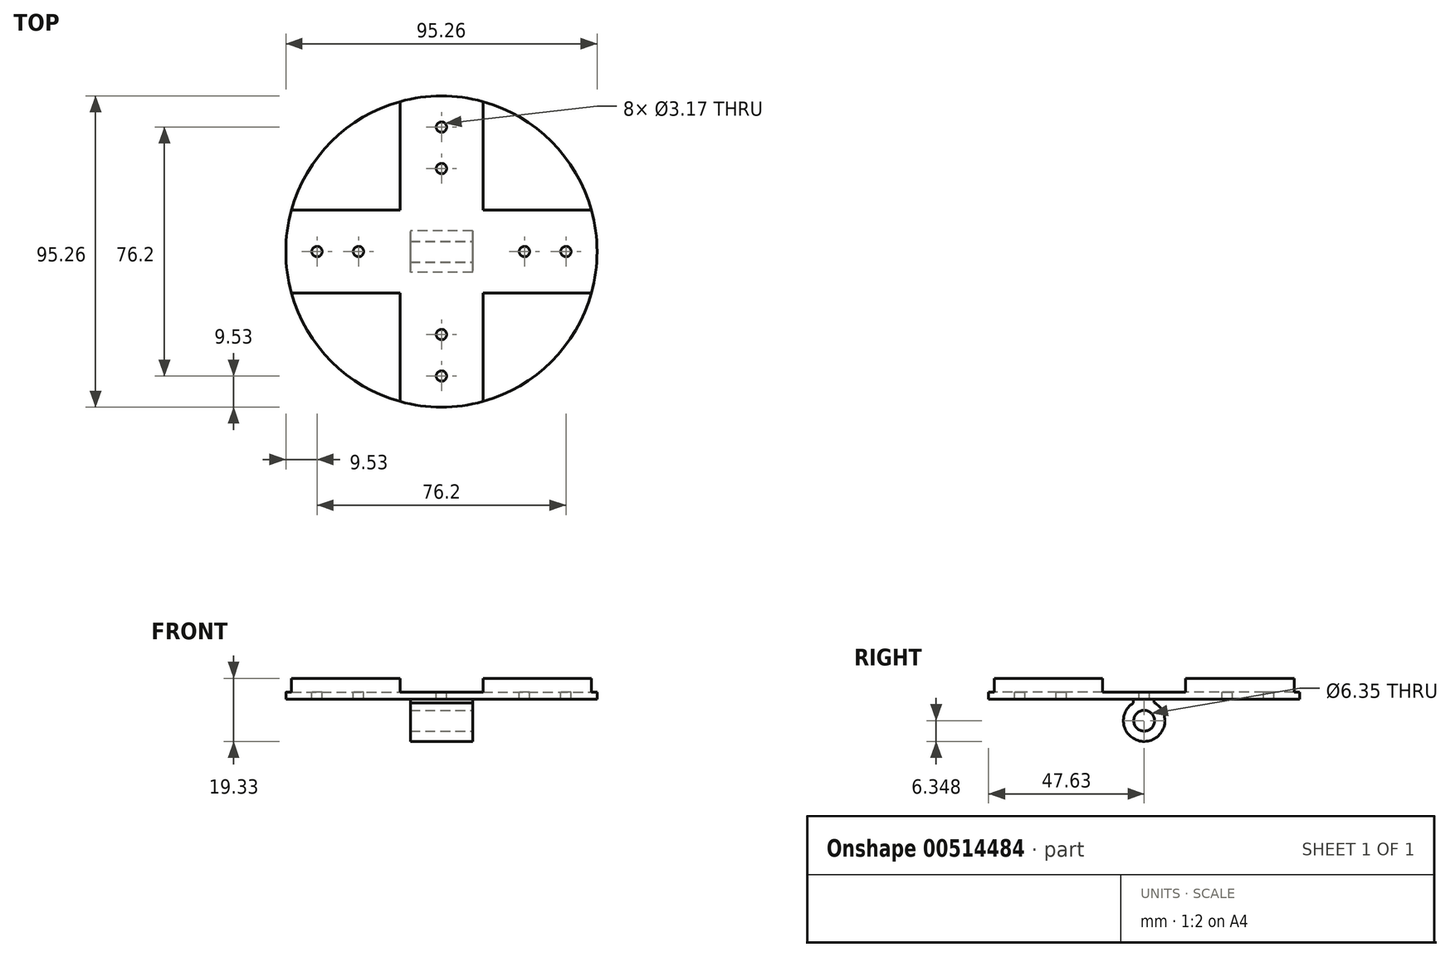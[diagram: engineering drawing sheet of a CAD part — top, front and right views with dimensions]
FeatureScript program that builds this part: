
annotation { "Feature Type Name" : "Feature", "Feature Type Description" : "" }
export const myFeature = defineFeature(function(context is Context, id is Id, definition is map)
    precondition{}
    {
        {
            var Q0;
            Q0=qCreatedBy(makeId("Top.planeOp"),FACE);
            var sketch = newSketch(context, id + "F0", { "sketchPlane" : qUnion([Q0])});
            skCircle(sketch, "E0", {"center": v(0, 0) * mm, "radius": 47.63 * mm});
            skSolve(sketch);
        }
        {
            var Q0;
            Q0=makeQuery(id+"F0.imprint","IMPRINT",FACE,{"disambiguationData":[TD([[makeQuery(id+"F0.imprint","IMPRINT",EDGE,{"derivedFrom":sQuery(id+"F0.wireOp",EDGE,"E0")}),1.0]])]});
            extrude(context, id + "F1", {"entities" : qUnion([Q0]), "depth" : 6.35 * mm});
        }
        {
            var Q0;
            Q0=makeQuery(id+"F1.opExtrude","CAP_FACE",FACE,{"disambiguationData":[OSD([sQuery(id+"F0.wireOp",EDGE,"E0")])],"isStart":false});
            var sketch = newSketch(context, id + "F2", { "sketchPlane" : qUnion([Q0])});
            skLineSegment(sketch, "E1.bottom", {"start": v(-12.7, 57.15) * mm, "end": v(12.7, 57.15) * mm});
            skLineSegment(sketch, "E1.top", {"start": v(-12.7, -57.15) * mm, "end": v(12.7, -57.15) * mm});
            skLineSegment(sketch, "E1.left", {"start": v(-12.7, 57.15) * mm, "end": v(-12.7, 12.7) * mm});
            skLineSegment(sketch, "E1.right", {"start": v(12.7, 57.15) * mm, "end": v(12.7, 12.7) * mm});
            skLineSegment(sketch, "E2.bottom", {"start": v(-57.15, 12.7) * mm, "end": v(-12.7, 12.7) * mm});
            skLineSegment(sketch, "E2.top", {"start": v(-57.15, -12.7) * mm, "end": v(-12.7, -12.7) * mm});
            skLineSegment(sketch, "E2.left", {"start": v(-57.15, 12.7) * mm, "end": v(-57.15, -12.7) * mm});
            skLineSegment(sketch, "E2.right", {"start": v(57.15, 12.7) * mm, "end": v(57.15, -12.7) * mm});
            skLineSegment(sketch, "E3.trimOffspring", {"start": v(-12.7, -12.7) * mm, "end": v(-12.7, -57.15) * mm});
            skLineSegment(sketch, "E4.trimOffspring", {"start": v(12.7, -12.7) * mm, "end": v(57.15, -12.7) * mm});
            skLineSegment(sketch, "E5.trimOffspring", {"start": v(12.7, -12.7) * mm, "end": v(12.7, -57.15) * mm});
            skLineSegment(sketch, "E6.trimOffspring", {"start": v(12.7, 12.7) * mm, "end": v(57.15, 12.7) * mm});
            skSolve(sketch);
        }
        {
            var Q0;
            {var subQ0=sQuery(id+"F2.wireOp",EDGE,"E1.left");var subQ9=sQuery(id+"F2.wireOp",EDGE,"E2.bottom");var subQ16=makeQuery(id+"F2.imprint","INTERSECT",VERTEX,{"derivedFrom":[subQ0,subQ9]});Q0=makeQuery(id+"F2.imprint","IMPRINT",FACE,{"disambiguationData":[TD([[makeQuery(id+"F2.imprint","IMPRINT",EDGE,{"disambiguationData":[TD([[subQ16,1.0]])],"derivedFrom":subQ0}),1.0]])]});}
            extrude(context, id + "F3", {"entities" : qUnion([Q0]), "operationType" : NewBodyOperationType.REMOVE, "oppositeDirection" : true, "depth" : 4.25 * mm});
        }
        {
            var Q0;
            Q0=makeQuery(id+"F3.boolean.opBoolean","COPY",FACE,{"derivedFrom":makeQuery(id+"F3.opExtrude","CAP_FACE",FACE,{"disambiguationData":[OSD([sQuery(id+"F0.wireOp",EDGE,"E0"),sQuery(id+"F2.wireOp",EDGE,"E1.left"),sQuery(id+"F2.wireOp",EDGE,"E1.right"),sQuery(id+"F2.wireOp",EDGE,"E2.bottom"),sQuery(id+"F2.wireOp",EDGE,"E2.top"),sQuery(id+"F2.wireOp",EDGE,"E3.trimOffspring"),sQuery(id+"F2.wireOp",EDGE,"E4.trimOffspring"),sQuery(id+"F2.wireOp",EDGE,"E5.trimOffspring"),sQuery(id+"F2.wireOp",EDGE,"E6.trimOffspring")])],"isStart":false})});
            var sketch = newSketch(context, id + "F4", { "sketchPlane" : qUnion([Q0])});
            skLineSegment(sketch, "E7", {"start": v(0, 47.63) * mm, "end": v(0, -47.63) * mm, "construction": true});
            skLineSegment(sketch, "E8", {"start": v(-47.62, 0) * mm, "end": v(47.62, 0) * mm, "construction": true});
            skLineSegment(sketch, "E9", {"start": v(-45.9, 12.7) * mm, "end": v(45.9, 12.7) * mm, "construction": true});
            skLineSegment(sketch, "E10", {"start": v(-45.9, -12.7) * mm, "end": v(45.9, -12.7) * mm, "construction": true});
            skLineSegment(sketch, "E11", {"start": v(-12.7, -45.9) * mm, "end": v(-12.7, 45.9) * mm, "construction": true});
            skLineSegment(sketch, "E12", {"start": v(12.7, -45.9) * mm, "end": v(12.7, 45.9) * mm, "construction": true});
            skCircle(sketch, "E13", {"center": v(0, -25.4) * mm, "radius": 1.59 * mm});
            skCircle(sketch, "E14", {"center": v(0, -38.1) * mm, "radius": 1.59 * mm});
            skCircle(sketch, "E15", {"center": v(25.4, 0) * mm, "radius": 1.59 * mm});
            skCircle(sketch, "E16", {"center": v(38.1, 0) * mm, "radius": 1.59 * mm});
            skCircle(sketch, "E17", {"center": v(0, 25.4) * mm, "radius": 1.59 * mm});
            skCircle(sketch, "E18", {"center": v(0, 38.1) * mm, "radius": 1.59 * mm});
            skCircle(sketch, "E19", {"center": v(-25.4, 0) * mm, "radius": 1.59 * mm});
            skCircle(sketch, "E20", {"center": v(-38.1, 0) * mm, "radius": 1.59 * mm});
            skPoint(sketch, "E21.top.start.orphan", {"position": v(-38.1, -3.17) * mm});
            skPoint(sketch, "E22.orphan", {"position": v(-25.4, -3.18) * mm});
            skPoint(sketch, "E21.bottom.end.orphan", {"position": v(-25.4, 3.18) * mm});
            skPoint(sketch, "E21.left.start.orphan", {"position": v(-38.1, 3.17) * mm});
            skPoint(sketch, "E23.top.start.orphan", {"position": v(25.4, -3.17) * mm});
            skPoint(sketch, "E24.orphan", {"position": v(38.1, -3.17) * mm});
            skPoint(sketch, "E23.bottom.end.orphan", {"position": v(38.1, 3.18) * mm});
            skPoint(sketch, "E23.left.start.orphan", {"position": v(25.4, 3.18) * mm});
            skPoint(sketch, "E25.left.end.orphan", {"position": v(-3.17, -38.1) * mm});
            skPoint(sketch, "E25.right.end.orphan", {"position": v(3.18, -38.1) * mm});
            skPoint(sketch, "E26.orphan", {"position": v(3.18, -25.4) * mm});
            skPoint(sketch, "E25.bottom.start.orphan", {"position": v(-3.17, -25.4) * mm});
            skPoint(sketch, "E27.left.end.orphan", {"position": v(-3.18, 25.4) * mm});
            skPoint(sketch, "E27.right.end.orphan", {"position": v(3.17, 25.4) * mm});
            skPoint(sketch, "E28.orphan", {"position": v(3.17, 38.1) * mm});
            skPoint(sketch, "E27.bottom.start.orphan", {"position": v(-3.18, 38.1) * mm});
            skSolve(sketch);
        }
        {
            var Q0;
            Q0=makeQuery(id+"F1.opExtrude","CAP_FACE",FACE,{"disambiguationData":[OSD([sQuery(id+"F0.wireOp",EDGE,"E0")])],"isStart":true});
            var sketch = newSketch(context, id + "F5", { "sketchPlane" : qUnion([Q0])});
            skLineSegment(sketch, "E29.bottom", {"start": v(-9.53, 3.3) * mm, "end": v(9.53, 3.3) * mm});
            skLineSegment(sketch, "E29.top", {"start": v(-9.53, -3.04) * mm, "end": v(9.53, -3.04) * mm});
            skLineSegment(sketch, "E29.left", {"start": v(-9.53, 3.3) * mm, "end": v(-9.53, -3.04) * mm});
            skLineSegment(sketch, "E29.right", {"start": v(9.53, 3.3) * mm, "end": v(9.53, -3.04) * mm});
            skSolve(sketch);
        }
        {
            var Q0;
            Q0=makeQuery(id+"F5.imprint","IMPRINT",FACE,{"disambiguationData":[TD([[makeQuery(id+"F5.imprint","IMPRINT",EDGE,{"derivedFrom":sQuery(id+"F5.wireOp",EDGE,"E29.bottom")}),-1.0]])]});
            extrude(context, id + "F6", {"entities" : qUnion([Q0]), "operationType" : NewBodyOperationType.ADD, "depth" : 6.35 * mm});
        }
        {
            var Q0;
            Q0=makeQuery(id+"F6.opExtrude","SWEPT_FACE",FACE,{"disambiguationData":[OSD([sQuery(id+"F5.wireOp",EDGE,"E29.left")])]});
            var sketch = newSketch(context, id + "F7", { "sketchPlane" : qUnion([Q0])});
            skCircle(sketch, "E30", {"center": v(0, -6.63) * mm, "radius": 6.35 * mm});
            skSolve(sketch);
        }
        {
            var Q0;
            {var subQ1=sQuery(id+"F5.wireOp",EDGE,"E29.left");var subQ6=makeQuery(id+"F6.opExtrude","CAP_EDGE",EDGE,{"disambiguationData":[OSD([subQ1])],"isStart":false});Q0=makeQuery(id+"F7.imprint","IMPRINT",FACE,{"disambiguationData":[TD([[makeQuery(id+"F7.imprint","IMPRINT",EDGE,{"derivedFrom":subQ6}),1.0]])]});}
            extrude(context, id + "F8", {"entities" : qUnion([Q0]), "operationType" : NewBodyOperationType.ADD, "oppositeDirection" : true, "depth" : 19.05 * mm});
        }
        {
            var Q0;
            Q0=makeQuery(id+"F8.boolean.opBoolean","MERGE",FACE,{"derivedFrom":[makeQuery(id+"F6.opExtrude","SWEPT_FACE",FACE,{"disambiguationData":[OSD([sQuery(id+"F5.wireOp",EDGE,"E29.right")])]}),makeQuery(id+"F8.opExtrude","CAP_FACE",FACE,{"disambiguationData":[OSD([sQuery(id+"F5.wireOp",EDGE,"E29.bottom"),sQuery(id+"F5.wireOp",EDGE,"E29.top"),sQuery(id+"F5.wireOp",EDGE,"E29.left"),sQuery(id+"F7.wireOp",EDGE,"E30")])],"isStart":false})]});
            var sketch = newSketch(context, id + "F9", { "sketchPlane" : qUnion([Q0])});
            skCircle(sketch, "E31", {"center": v(0, -6.63) * mm, "radius": 3.18 * mm});
            skSolve(sketch);
        }
        {
            var Q0;
            Q0=makeQuery(id+"F9.imprint","IMPRINT",FACE,{"disambiguationData":[TD([[makeQuery(id+"F9.imprint","IMPRINT",EDGE,{"derivedFrom":sQuery(id+"F9.wireOp",EDGE,"E31")}),1.0]])]});
            extrude(context, id + "F10", {"entities" : qUnion([Q0]), "operationType" : NewBodyOperationType.REMOVE, "oppositeDirection" : true, "depth" : 19.05 * mm});
        }
        {
            var Q0;
            Q0=makeQuery(id+"F4.imprint","IMPRINT",FACE,{"disambiguationData":[TD([[makeQuery(id+"F4.imprint","IMPRINT",EDGE,{"derivedFrom":sQuery(id+"F4.wireOp",EDGE,"E20")}),1.0]])]});
            var Q1;
            Q1=makeQuery(id+"F4.imprint","IMPRINT",FACE,{"disambiguationData":[TD([[makeQuery(id+"F4.imprint","IMPRINT",EDGE,{"derivedFrom":sQuery(id+"F4.wireOp",EDGE,"E19")}),1.0]])]});
            var Q2;
            Q2=makeQuery(id+"F4.imprint","IMPRINT",FACE,{"disambiguationData":[TD([[makeQuery(id+"F4.imprint","IMPRINT",EDGE,{"derivedFrom":sQuery(id+"F4.wireOp",EDGE,"E13")}),1.0]])]});
            var Q3;
            Q3=makeQuery(id+"F4.imprint","IMPRINT",FACE,{"disambiguationData":[TD([[makeQuery(id+"F4.imprint","IMPRINT",EDGE,{"derivedFrom":sQuery(id+"F4.wireOp",EDGE,"E14")}),1.0]])]});
            var Q4;
            Q4=makeQuery(id+"F4.imprint","IMPRINT",FACE,{"disambiguationData":[TD([[makeQuery(id+"F4.imprint","IMPRINT",EDGE,{"derivedFrom":sQuery(id+"F4.wireOp",EDGE,"E15")}),1.0]])]});
            var Q5;
            Q5=makeQuery(id+"F4.imprint","IMPRINT",FACE,{"disambiguationData":[TD([[makeQuery(id+"F4.imprint","IMPRINT",EDGE,{"derivedFrom":sQuery(id+"F4.wireOp",EDGE,"E16")}),1.0]])]});
            var Q6;
            Q6=makeQuery(id+"F4.imprint","IMPRINT",FACE,{"disambiguationData":[TD([[makeQuery(id+"F4.imprint","IMPRINT",EDGE,{"derivedFrom":sQuery(id+"F4.wireOp",EDGE,"E17")}),1.0]])]});
            var Q7;
            Q7=makeQuery(id+"F4.imprint","IMPRINT",FACE,{"disambiguationData":[TD([[makeQuery(id+"F4.imprint","IMPRINT",EDGE,{"derivedFrom":sQuery(id+"F4.wireOp",EDGE,"E18")}),1.0]])]});
            extrude(context, id + "F11", {"entities" : qUnion([Q0, Q1, Q2, Q3, Q4, Q5, Q6, Q7]), "operationType" : NewBodyOperationType.REMOVE, "oppositeDirection" : true, "depth" : 25.4 * mm});
        }
    });
